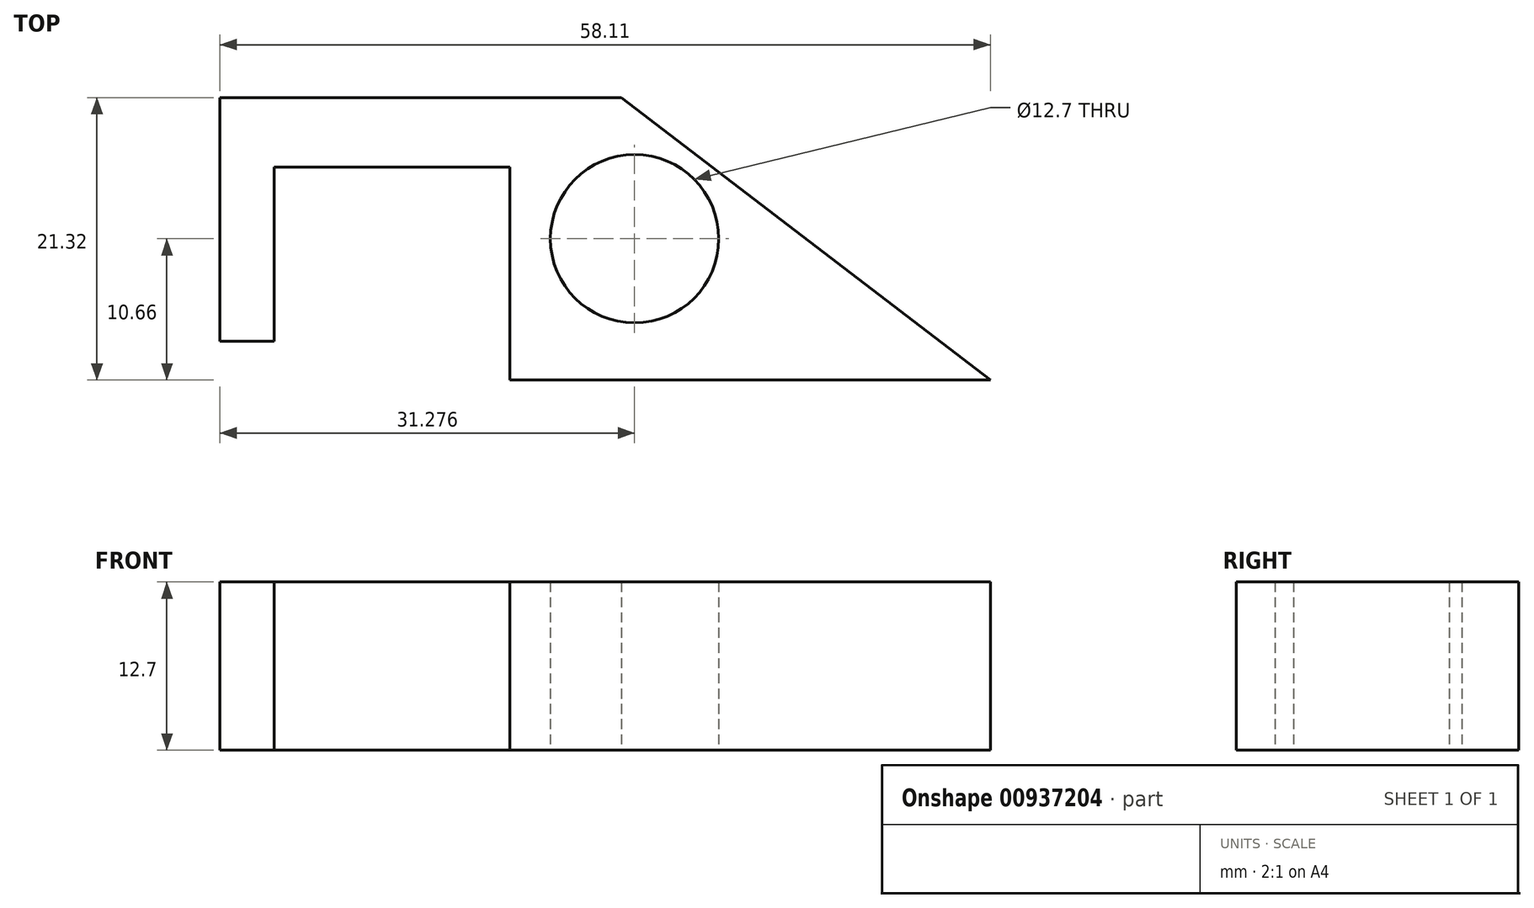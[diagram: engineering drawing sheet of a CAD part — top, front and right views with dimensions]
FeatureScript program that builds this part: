
annotation { "Feature Type Name" : "Feature", "Feature Type Description" : "" }
export const myFeature = defineFeature(function(context is Context, id is Id, definition is map)
    precondition{}
    {
        {
            var Q0;
            Q0=qCreatedBy(makeId("Top.planeOp"),FACE);
            var sketch = newSketch(context, id + "F0", { "sketchPlane" : qUnion([Q0])});
            skLineSegment(sketch, "E0", {"start": v(-44.87, 0) * mm, "end": v(-44.87, 5.24) * mm});
            skLineSegment(sketch, "E1", {"start": v(-44.87, 5.24) * mm, "end": v(-40.78, 5.24) * mm});
            skLineSegment(sketch, "E2", {"start": v(-40.78, 5.24) * mm, "end": v(-23.01, 5.24) * mm});
            skLineSegment(sketch, "E3", {"start": v(-23.01, 5.24) * mm, "end": v(13.24, 5.24) * mm});
            skLineSegment(sketch, "E4", {"start": v(13.24, 5.24) * mm, "end": v(13.24, -16.08) * mm});
            skLineSegment(sketch, "E5", {"start": v(13.24, -16.08) * mm, "end": v(-23.01, -16.08) * mm});
            skLineSegment(sketch, "E6", {"start": v(-23.01, -16.08) * mm, "end": v(-23.01, 0) * mm});
            skLineSegment(sketch, "E7", {"start": v(-23.01, 0) * mm, "end": v(-40.78, 0) * mm});
            skLineSegment(sketch, "E8", {"start": v(-40.78, 0) * mm, "end": v(-40.78, -4.35) * mm});
            skLineSegment(sketch, "E9", {"start": v(-40.78, -4.35) * mm, "end": v(-44.87, -4.35) * mm});
            skLineSegment(sketch, "E10", {"start": v(-44.87, -4.35) * mm, "end": v(-44.87, 0) * mm});
            skCircle(sketch, "E11", {"center": v(-13.6, -5.42) * mm, "radius": 6.35 * mm});
            skSolve(sketch);
        }
        {
            var Q0;
            Q0=makeQuery(id+"F0.imprint","IMPRINT",FACE,{"disambiguationData":[TD([[makeQuery(id+"F0.imprint","IMPRINT",EDGE,{"derivedFrom":sQuery(id+"F0.wireOp",EDGE,"E0")}),-1.0]])]});
            extrude(context, id + "F1", {"entities" : qUnion([Q0]), "depth" : 12.7 * mm, "offsetDistance" : 25.4 * mm});
        }
        {
            var Q0;
            Q0=makeQuery(id+"F1.opExtrude","SWEPT_FACE",FACE,{"disambiguationData":[OSD([sQuery(id+"F0.wireOp",EDGE,"E9")])]});
            var sketch = newSketch(context, id + "F2", { "sketchPlane" : qUnion([Q0])});
            skLineSegment(sketch, "E12.bottom", {"start": v(-44.87, 0) * mm, "end": v(-40.78, 0) * mm});
            skLineSegment(sketch, "E12.top", {"start": v(-44.87, 12.7) * mm, "end": v(-40.78, 12.7) * mm});
            skLineSegment(sketch, "E12.left", {"start": v(-44.87, 0) * mm, "end": v(-44.87, 12.7) * mm});
            skLineSegment(sketch, "E12.right", {"start": v(-40.78, 0) * mm, "end": v(-40.78, 12.7) * mm});
            skSolve(sketch);
        }
        {
            var Q0;
            Q0 = qSketchRegion(id + "F2", true);
            extrude(context, id + "F3", {"entities" : qUnion([Q0]), "operationType" : NewBodyOperationType.ADD, "depth" : 8.8 * mm, "offsetDistance" : 25.4 * mm});
        }
        {
            var Q0;
            Q0=makeQuery(id+"F3.boolean.opBoolean","MERGE",FACE,{"derivedFrom":[makeQuery(id+"F1.opExtrude","CAP_FACE",FACE,{"disambiguationData":[OSD([sQuery(id+"F0.wireOp",EDGE,"E0"),sQuery(id+"F0.wireOp",EDGE,"E1"),sQuery(id+"F0.wireOp",EDGE,"E2"),sQuery(id+"F0.wireOp",EDGE,"E3"),sQuery(id+"F0.wireOp",EDGE,"E4"),sQuery(id+"F0.wireOp",EDGE,"E5"),sQuery(id+"F0.wireOp",EDGE,"E6"),sQuery(id+"F0.wireOp",EDGE,"E7"),sQuery(id+"F0.wireOp",EDGE,"E8"),sQuery(id+"F0.wireOp",EDGE,"E9"),sQuery(id+"F0.wireOp",EDGE,"E10"),sQuery(id+"F0.wireOp",EDGE,"E11")])],"isStart":true}),makeQuery(id+"F3.opExtrude","SWEPT_FACE",FACE,{"disambiguationData":[OSD([sQuery(id+"F2.wireOp",EDGE,"E12.bottom")])]})]});
            var sketch = newSketch(context, id + "F4", { "sketchPlane" : qUnion([Q0])});
            skLineSegment(sketch, "E13", {"start": v(13.24, 16.08) * mm, "end": v(-14.6, -5.24) * mm});
            skLineSegment(sketch, "E14", {"start": v(-14.6, -5.24) * mm, "end": v(13.24, -5.24) * mm});
            skLineSegment(sketch, "E15", {"start": v(13.24, -5.24) * mm, "end": v(13.24, 16.08) * mm});
            skSolve(sketch);
        }
        {
            var Q0;
            Q0 = qSketchRegion(id + "F4", true);
            extrude(context, id + "F5", {"entities" : qUnion([Q0]), "operationType" : NewBodyOperationType.REMOVE, "endBound" : BoundingType.THROUGH_ALL, "oppositeDirection" : true, "depth" : 25.4 * mm, "offsetDistance" : 25.4 * mm});
        }
    });
